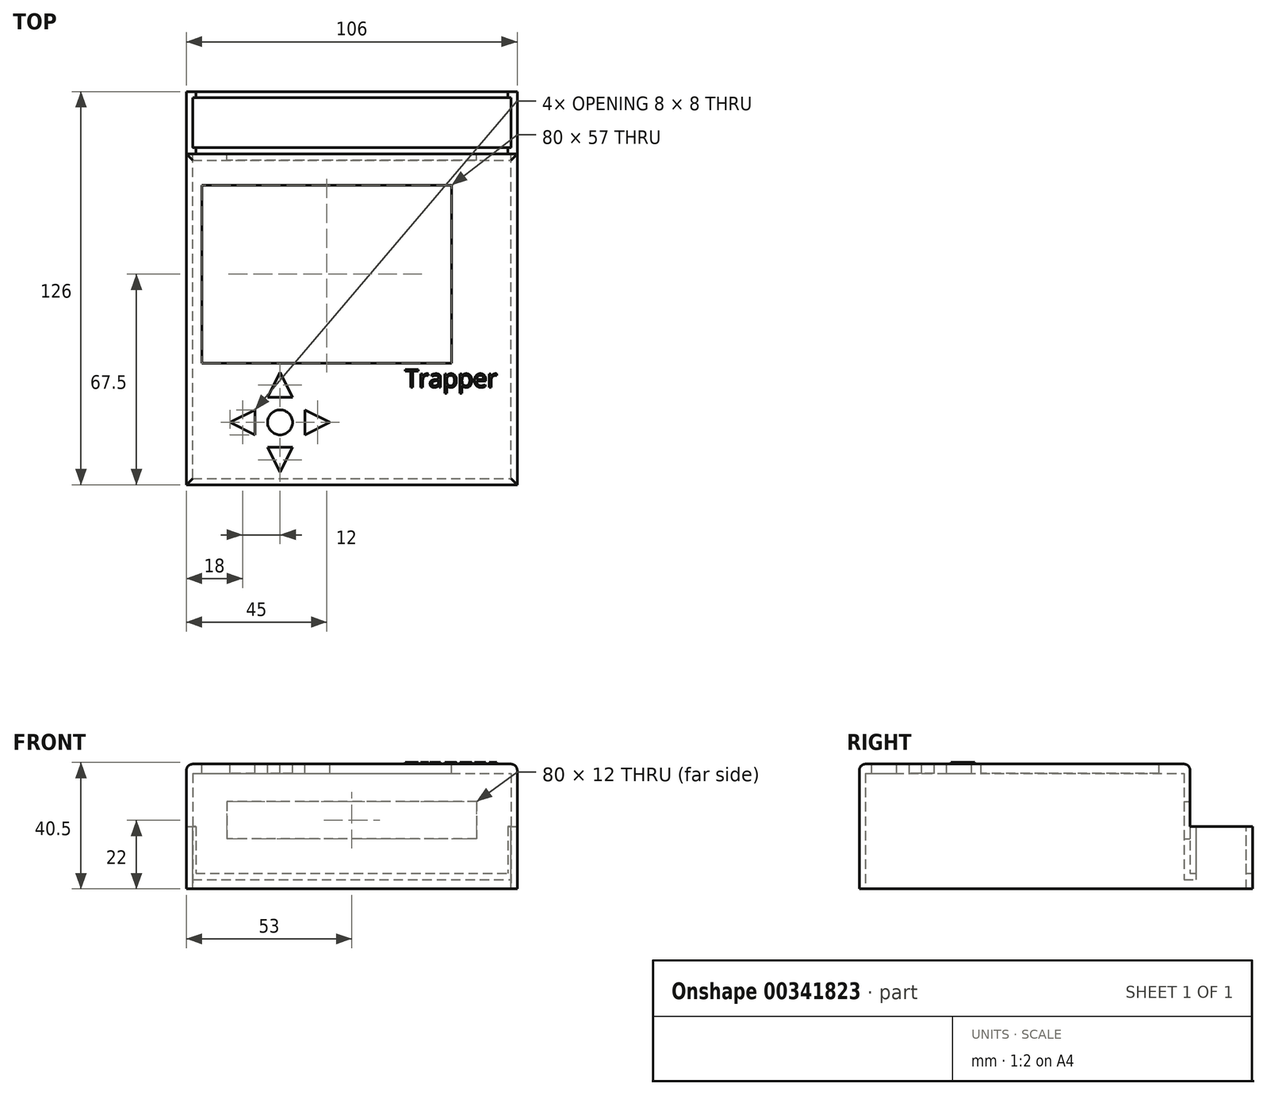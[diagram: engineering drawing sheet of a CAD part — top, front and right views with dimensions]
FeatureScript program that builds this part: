
annotation { "Feature Type Name" : "Feature", "Feature Type Description" : "" }
export const myFeature = defineFeature(function(context is Context, id is Id, definition is map)
    precondition{}
    {
        {
            var Q0;
            Q0=qCreatedBy(makeId("Top.planeOp"),FACE);
            var sketch = newSketch(context, id + "F0", { "sketchPlane" : qUnion([Q0])});
            skLineSegment(sketch, "E0.bottom", {"start": v(0, 106) * mm, "end": v(106, 106) * mm});
            skLineSegment(sketch, "E0.top", {"start": v(0, 0) * mm, "end": v(106, 0) * mm});
            skLineSegment(sketch, "E0.left", {"start": v(0, 106) * mm, "end": v(0, 0) * mm});
            skLineSegment(sketch, "E0.right", {"start": v(106, 106) * mm, "end": v(106, 0) * mm});
            skSolve(sketch);
        }
        {
            var Q0;
            Q0=makeQuery(id+"F0.imprint","IMPRINT",FACE,{"disambiguationData":[TD([[makeQuery(id+"F0.imprint","IMPRINT",EDGE,{"derivedFrom":sQuery(id+"F0.wireOp",EDGE,"E0.bottom")}),-1.0]])]});
            extrude(context, id + "F1", {"entities" : qUnion([Q0]), "depth" : 40 * mm});
        }
        {
            var Q0;
            Q0=makeQuery(id+"F1.opExtrude","CAP_FACE",FACE,{"disambiguationData":[OSD([sQuery(id+"F0.wireOp",EDGE,"E0.bottom"),sQuery(id+"F0.wireOp",EDGE,"E0.top"),sQuery(id+"F0.wireOp",EDGE,"E0.left"),sQuery(id+"F0.wireOp",EDGE,"E0.right")])],"isStart":true});
            var sketch = newSketch(context, id + "F2", { "sketchPlane" : qUnion([Q0])});
            skLineSegment(sketch, "E1.bottom", {"start": v(2, -2) * mm, "end": v(104, -2) * mm});
            skLineSegment(sketch, "E1.top", {"start": v(2, -104) * mm, "end": v(104, -104) * mm});
            skLineSegment(sketch, "E1.left", {"start": v(2, -2) * mm, "end": v(2, -104) * mm});
            skLineSegment(sketch, "E1.right", {"start": v(104, -2) * mm, "end": v(104, -104) * mm});
            skSolve(sketch);
        }
        {
            var Q0;
            Q0 = qSketchRegion(id + "F2", true);
            extrude(context, id + "F3", {"entities" : qUnion([Q0]), "operationType" : NewBodyOperationType.REMOVE, "oppositeDirection" : true, "depth" : 37 * mm});
        }
        {
            var Q0;
            Q0=makeQuery(id+"F1.opExtrude","CAP_FACE",FACE,{"disambiguationData":[OSD([sQuery(id+"F0.wireOp",EDGE,"E0.bottom"),sQuery(id+"F0.wireOp",EDGE,"E0.top"),sQuery(id+"F0.wireOp",EDGE,"E0.left"),sQuery(id+"F0.wireOp",EDGE,"E0.right")])],"isStart":false});
            var sketch = newSketch(context, id + "F4", { "sketchPlane" : qUnion([Q0])});
            skLineSegment(sketch, "E2.bottom", {"start": v(5, 96) * mm, "end": v(85, 96) * mm});
            skLineSegment(sketch, "E2.top", {"start": v(5, 39) * mm, "end": v(85, 39) * mm});
            skLineSegment(sketch, "E2.left", {"start": v(5, 96) * mm, "end": v(5, 39) * mm});
            skLineSegment(sketch, "E2.right", {"start": v(85, 96) * mm, "end": v(85, 39) * mm});
            skLineSegment(sketch, "E3", {"start": v(30, 63.07) * mm, "end": v(30, -7.07) * mm, "construction": true});
            skLineSegment(sketch, "E4", {"start": v(-11.84, 20) * mm, "end": v(91.74, 20) * mm, "construction": true});
            skCircle(sketch, "E5", {"center": v(30, 20) * mm, "radius": 4 * mm});
            skLineSegment(sketch, "E6", {"start": v(38, 24) * mm, "end": v(38, 16) * mm});
            skLineSegment(sketch, "E7", {"start": v(38, 16) * mm, "end": v(46, 20) * mm});
            skLineSegment(sketch, "E8", {"start": v(46, 20) * mm, "end": v(38, 24) * mm});
            skLineSegment(sketch, "E9", {"start": v(26, 28) * mm, "end": v(34, 28) * mm});
            skPoint(sketch, "E9.startSnap0", {"position": v(30, 28) * mm});
            skLineSegment(sketch, "E10", {"start": v(34, 28) * mm, "end": v(30, 36) * mm});
            skLineSegment(sketch, "E11", {"start": v(30, 36) * mm, "end": v(26, 28) * mm});
            skLineSegment(sketch, "E12", {"start": v(22, 16) * mm, "end": v(22, 24) * mm});
            skLineSegment(sketch, "E13", {"start": v(22, 24) * mm, "end": v(14, 20) * mm});
            skLineSegment(sketch, "E14", {"start": v(14, 20) * mm, "end": v(22, 16) * mm});
            skLineSegment(sketch, "E15", {"start": v(26, 12) * mm, "end": v(34, 12) * mm});
            skLineSegment(sketch, "E16", {"start": v(34, 12) * mm, "end": v(30, 4) * mm});
            skLineSegment(sketch, "E17", {"start": v(30, 4) * mm, "end": v(26, 12) * mm});
            skSolve(sketch);
        }
        {
            var Q0;
            Q0 = qSketchRegion(id + "F4", true);
            extrude(context, id + "F5", {"entities" : qUnion([Q0]), "operationType" : NewBodyOperationType.REMOVE, "endBound" : BoundingType.UP_TO_NEXT, "oppositeDirection" : true, "depth" : 25 * mm});
        }
        {
            var Q0;
            Q0=makeQuery(id+"F1.opExtrude","CAP_EDGE",EDGE,{"disambiguationData":[OSD([sQuery(id+"F0.wireOp",EDGE,"E0.bottom")])],"isStart":false});
            var Q1;
            Q1=makeQuery(id+"F1.opExtrude","CAP_EDGE",EDGE,{"disambiguationData":[OSD([sQuery(id+"F0.wireOp",EDGE,"E0.left")])],"isStart":false});
            var Q2;
            Q2=makeQuery(id+"F1.opExtrude","CAP_EDGE",EDGE,{"disambiguationData":[OSD([sQuery(id+"F0.wireOp",EDGE,"E0.top")])],"isStart":false});
            var Q3;
            Q3=makeQuery(id+"F1.opExtrude","CAP_EDGE",EDGE,{"disambiguationData":[OSD([sQuery(id+"F0.wireOp",EDGE,"E0.right")])],"isStart":false});
            fillet(context, id + "F6", {"entities" : qUnion([Q0, Q1, Q2, Q3]), "radius" : 2 * mm, "tangentPropagation" : true, "allowEdgeOverflow" : false});
        }
        {
            var Q0;
            Q0=makeQuery(id+"F1.opExtrude","CAP_FACE",FACE,{"disambiguationData":[OSD([sQuery(id+"F0.wireOp",EDGE,"E0.bottom"),sQuery(id+"F0.wireOp",EDGE,"E0.top"),sQuery(id+"F0.wireOp",EDGE,"E0.left"),sQuery(id+"F0.wireOp",EDGE,"E0.right")])],"isStart":false});
            var sketch = newSketch(context, id + "F7", { "sketchPlane" : qUnion([Q0])});
            skText(sketch, "E18", { "text": "Trapper", "fontName": "OpenSans-Regular.ttf"});
            const initialGuessF7  = {"E18": [0.07, 0.03126, 1, 0, 0.00574]};
            skSetInitialGuess(sketch, initialGuessF7);
            skSolve(sketch);
        }
        {
            var Q0;
            Q0 = qSketchRegion(id + "F7", true);
            extrude(context, id + "F8", {"entities" : qUnion([Q0]), "operationType" : NewBodyOperationType.ADD, "depth" : 0.5 * mm});
        }
        {
            var Q0;
            Q0=qCreatedBy(makeId("Right.planeOp"),FACE);
            var sketch = newSketch(context, id + "F9", { "sketchPlane" : qUnion([Q0])});
            skLineSegment(sketch, "E19", {"start": v(106, 0) * mm, "end": v(126, 0) * mm});
            skLineSegment(sketch, "E20", {"start": v(126, 0) * mm, "end": v(126, 20) * mm});
            skLineSegment(sketch, "E21", {"start": v(126, 20) * mm, "end": v(106, 20) * mm});
            skLineSegment(sketch, "E22", {"start": v(106, 20) * mm, "end": v(106, 0) * mm});
            skPoint(sketch, "E23.orphan", {"position": v(0, 0) * mm});
            skSolve(sketch);
        }
        {
            var Q0;
            Q0=makeQuery(id+"F9.imprint","IMPRINT",FACE,{"disambiguationData":[TD([[makeQuery(id+"F9.imprint","IMPRINT",EDGE,{"derivedFrom":sQuery(id+"F9.wireOp",EDGE,"E19")}),1.0]])]});
            extrude(context, id + "F10", {"entities" : qUnion([Q0]), "operationType" : NewBodyOperationType.ADD, "depth" : 106 * mm});
        }
        {
            var Q0;
            Q0=qCreatedBy(makeId("Top.planeOp"),FACE);
            var sketch = newSketch(context, id + "F11", { "sketchPlane" : qUnion([Q0])});
            skLineSegment(sketch, "E24.bottom", {"start": v(2, 124) * mm, "end": v(104, 124) * mm});
            skLineSegment(sketch, "E24.top", {"start": v(2, 108) * mm, "end": v(104, 108) * mm});
            skLineSegment(sketch, "E24.left", {"start": v(2, 124) * mm, "end": v(2, 108) * mm});
            skLineSegment(sketch, "E24.right", {"start": v(104, 124) * mm, "end": v(104, 108) * mm});
            skSolve(sketch);
        }
        {
            var Q0;
            Q0=makeQuery(id+"F11.imprint","IMPRINT",FACE,{"disambiguationData":[TD([[makeQuery(id+"F11.imprint","IMPRINT",EDGE,{"derivedFrom":sQuery(id+"F11.wireOp",EDGE,"E24.bottom")}),-1.0]])]});
            extrude(context, id + "F12", {"entities" : qUnion([Q0]), "operationType" : NewBodyOperationType.REMOVE, "oppositeDirection" : true, "depth" : 25 * mm, "hasSecondDirection" : true, "secondDirectionOppositeDirection" : false, "secondDirectionDepth" : 25 * mm});
        }
        {
            var Q0;
            Q0=makeQuery(id+"F10.opExtrude","SWEPT_FACE",FACE,{"disambiguationData":[OSD([sQuery(id+"F9.wireOp",EDGE,"E20")])]});
            var sketch = newSketch(context, id + "F13", { "sketchPlane" : qUnion([Q0])});
            skLineSegment(sketch, "E25.bottom", {"start": v(-3, 20) * mm, "end": v(-103, 20) * mm});
            skLineSegment(sketch, "E25.top", {"start": v(-3, 5) * mm, "end": v(-103, 5) * mm});
            skLineSegment(sketch, "E25.left", {"start": v(-3, 20) * mm, "end": v(-3, 5) * mm});
            skLineSegment(sketch, "E25.right", {"start": v(-103, 20) * mm, "end": v(-103, 5) * mm});
            skSolve(sketch);
        }
        {
            var Q0;
            Q0 = qSketchRegion(id + "F13", true);
            extrude(context, id + "F14", {"entities" : qUnion([Q0]), "operationType" : NewBodyOperationType.REMOVE, "oppositeDirection" : true, "depth" : 20 * mm});
        }
        {
            var Q0;
            Q0=makeQuery(id+"F10.boolean.opBoolean","MERGE",FACE,{"derivedFrom":[makeQuery(id+"F1.opExtrude","CAP_FACE",FACE,{"disambiguationData":[OSD([sQuery(id+"F0.wireOp",EDGE,"E0.bottom"),sQuery(id+"F0.wireOp",EDGE,"E0.top"),sQuery(id+"F0.wireOp",EDGE,"E0.left"),sQuery(id+"F0.wireOp",EDGE,"E0.right")])],"isStart":true}),makeQuery(id+"F10.opExtrude","SWEPT_FACE",FACE,{"disambiguationData":[OSD([sQuery(id+"F9.wireOp",EDGE,"E19")])]})]});
            var sketch = newSketch(context, id + "F15", { "sketchPlane" : qUnion([Q0])});
            skLineSegment(sketch, "E26.bottom", {"start": v(104, -104) * mm, "end": v(2, -104) * mm});
            skLineSegment(sketch, "E26.top", {"start": v(104, -108) * mm, "end": v(2, -108) * mm});
            skLineSegment(sketch, "E26.left", {"start": v(104, -104) * mm, "end": v(104, -108) * mm});
            skLineSegment(sketch, "E26.right", {"start": v(2, -104) * mm, "end": v(2, -108) * mm});
            skSolve(sketch);
        }
        {
            var Q0;
            Q0=makeQuery(id+"F15.imprint","IMPRINT",FACE,{"disambiguationData":[TD([[makeQuery(id+"F15.imprint","IMPRINT",EDGE,{"derivedFrom":sQuery(id+"F15.wireOp",EDGE,"E26.top")}),1.0]])]});
            extrude(context, id + "F16", {"entities" : qUnion([Q0]), "operationType" : NewBodyOperationType.REMOVE, "oppositeDirection" : true, "depth" : 3 * mm});
        }
        {
            var Q0;
            Q0=makeQuery(id+"F14.boolean.opBoolean","MERGE",FACE,{"derivedFrom":[makeQuery(id+"F1.opExtrude","SWEPT_FACE",FACE,{"disambiguationData":[OSD([sQuery(id+"F0.wireOp",EDGE,"E0.bottom")])]}),makeQuery(id+"F14.opExtrude","CAP_FACE",FACE,{"disambiguationData":[OSD([sQuery(id+"F13.wireOp",EDGE,"E25.bottom"),sQuery(id+"F13.wireOp",EDGE,"E25.top"),sQuery(id+"F13.wireOp",EDGE,"E25.left"),sQuery(id+"F13.wireOp",EDGE,"E25.right")])],"isStart":false})]});
            var sketch = newSketch(context, id + "F17", { "sketchPlane" : qUnion([Q0])});
            skLineSegment(sketch, "E27.bottom", {"start": v(-93, 28) * mm, "end": v(-13, 28) * mm});
            skLineSegment(sketch, "E27.top", {"start": v(-93, 16) * mm, "end": v(-13, 16) * mm});
            skLineSegment(sketch, "E27.left", {"start": v(-93, 28) * mm, "end": v(-93, 16) * mm});
            skLineSegment(sketch, "E27.right", {"start": v(-13, 28) * mm, "end": v(-13, 16) * mm});
            skSolve(sketch);
        }
        {
            var Q0;
            Q0=makeQuery(id+"F17.imprint","IMPRINT",FACE,{"disambiguationData":[TD([[makeQuery(id+"F17.imprint","IMPRINT",EDGE,{"derivedFrom":sQuery(id+"F17.wireOp",EDGE,"E27.bottom")}),-1.0]])]});
            extrude(context, id + "F18", {"entities" : qUnion([Q0]), "operationType" : NewBodyOperationType.REMOVE, "oppositeDirection" : true, "depth" : 5 * mm});
        }
    });
